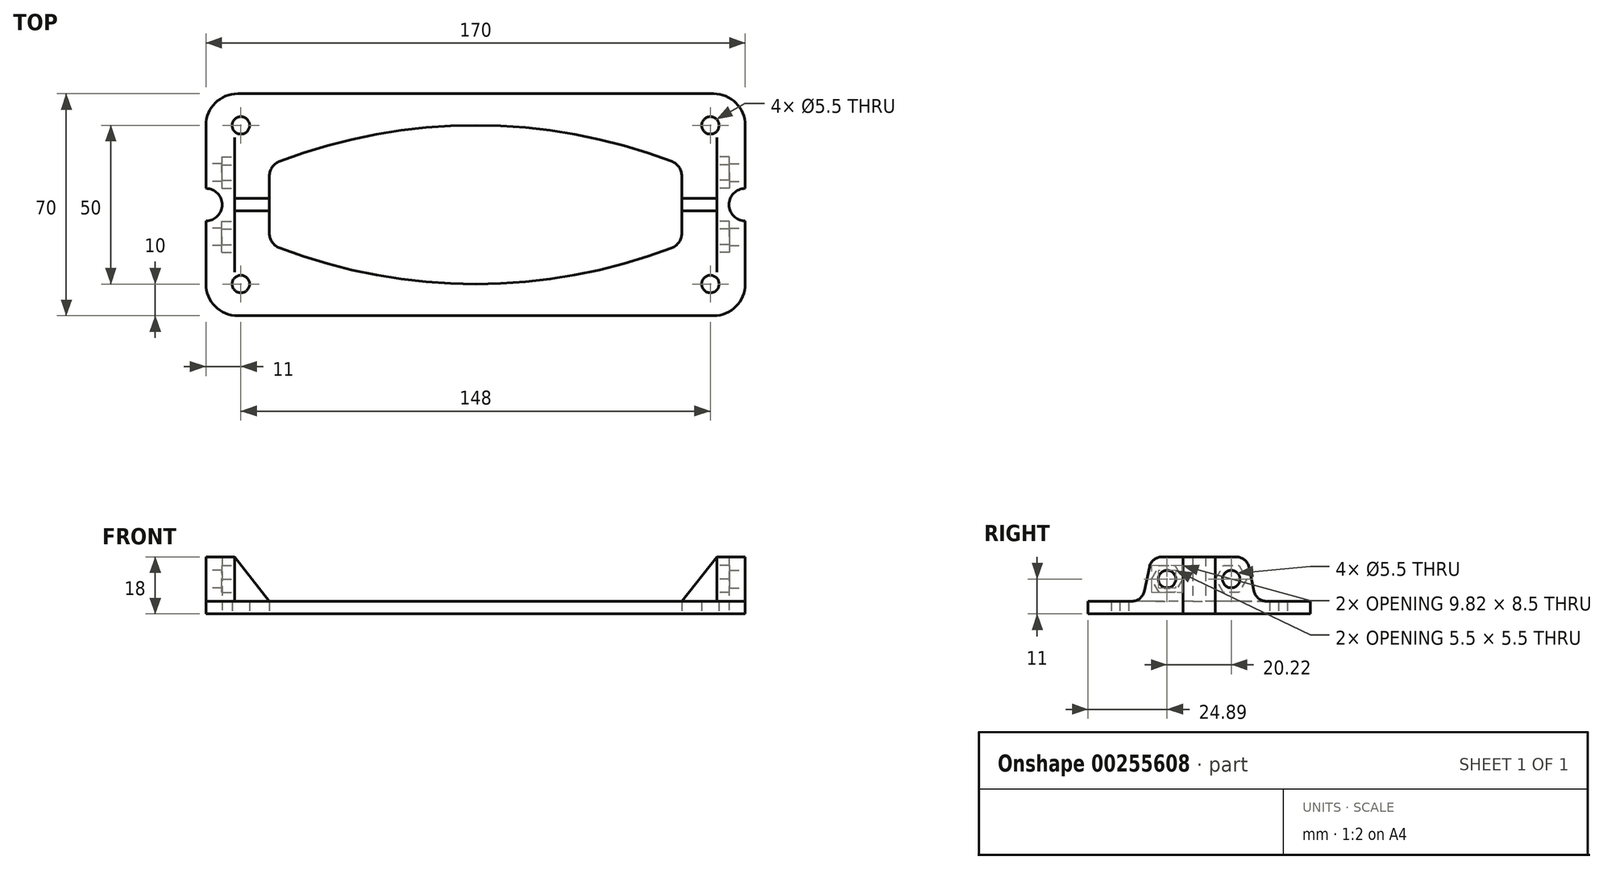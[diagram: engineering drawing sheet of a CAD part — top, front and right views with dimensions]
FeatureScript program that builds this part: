
annotation { "Feature Type Name" : "Feature", "Feature Type Description" : "" }
export const myFeature = defineFeature(function(context is Context, id is Id, definition is map)
    precondition{}
    {
        {
            var Q0;
            Q0=qCreatedBy(makeId("Top.planeOp"),FACE);
            var sketch = newSketch(context, id + "F0", { "sketchPlane" : qUnion([Q0])});
            skLineSegment(sketch, "E0.bottom", {"start": v(75, 35) * mm, "end": v(-75, 35) * mm});
            skLineSegment(sketch, "E0.top", {"start": v(75, -35) * mm, "end": v(-75, -35) * mm});
            skLineSegment(sketch, "E0.left", {"start": v(85, 25) * mm, "end": v(85, -25) * mm});
            skLineSegment(sketch, "E0.right", {"start": v(-85, 25) * mm, "end": v(-85, -25) * mm});
            skPoint(sketch, "E0.middle", {"position": v(0, 0) * mm});
            skLineSegment(sketch, "E1.left", {"start": v(65, 9) * mm, "end": v(65, -9) * mm});
            skLineSegment(sketch, "E1.right", {"start": v(-65, 9) * mm, "end": v(-65, -9) * mm});
            skLineSegment(sketch, "E2.bottom", {"start": v(-74, 25) * mm, "end": v(74, 25) * mm, "construction": true});
            skLineSegment(sketch, "E2.top", {"start": v(-74, -25) * mm, "end": v(74, -25) * mm, "construction": true});
            skLineSegment(sketch, "E2.left", {"start": v(-74, 25) * mm, "end": v(-74, -25) * mm, "construction": true});
            skLineSegment(sketch, "E2.right", {"start": v(74, 25) * mm, "end": v(74, -25) * mm, "construction": true});
            skCircle(sketch, "E3", {"center": v(-74, 25) * mm, "radius": 2.75 * mm});
            skCircle(sketch, "E4", {"center": v(74, 25) * mm, "radius": 2.75 * mm});
            skCircle(sketch, "E5", {"center": v(74, -25) * mm, "radius": 2.75 * mm});
            skCircle(sketch, "E6", {"center": v(-74, -25) * mm, "radius": 2.75 * mm});
            skPoint(sketch, "E7.visualSharp", {"position": v(-85, 35) * mm});
            skArc(sketch, "E7.filletArc", {"start": v(-75, 35) * mm, "mid": v(-82.07, 32.07) * mm, "end": v(-85, 25) * mm});
            skPoint(sketch, "E8.visualSharp", {"position": v(-85, -35) * mm});
            skArc(sketch, "E8.filletArc", {"start": v(-85, -25) * mm, "mid": v(-82.07, -32.07) * mm, "end": v(-75, -35) * mm});
            skPoint(sketch, "E9.visualSharp", {"position": v(85, -35) * mm});
            skArc(sketch, "E9.filletArc", {"start": v(75, -35) * mm, "mid": v(82.07, -32.07) * mm, "end": v(85, -25) * mm});
            skPoint(sketch, "E10.visualSharp", {"position": v(85, 35) * mm});
            skArc(sketch, "E10.filletArc", {"start": v(85, 25) * mm, "mid": v(82.07, 32.07) * mm, "end": v(75, 35) * mm});
            skArc(sketch, "E11", {"start": v(61.77, 13.67) * mm, "mid": v(0, 25) * mm, "end": v(-61.77, 13.67) * mm});
            skArc(sketch, "E12", {"start": v(-61.77, -13.67) * mm, "mid": v(0, -25) * mm, "end": v(61.77, -13.67) * mm});
            skPoint(sketch, "E13.visualSharp", {"position": v(-65, 12.41) * mm});
            skArc(sketch, "E13.filletArc", {"start": v(-61.77, 13.67) * mm, "mid": v(-64.12, 11.84) * mm, "end": v(-65, 9) * mm});
            skPoint(sketch, "E14.visualSharp", {"position": v(-65, -12.41) * mm});
            skArc(sketch, "E14.filletArc", {"start": v(-65, -9) * mm, "mid": v(-64.12, -11.84) * mm, "end": v(-61.77, -13.67) * mm});
            skPoint(sketch, "E15.visualSharp", {"position": v(65, -12.41) * mm});
            skArc(sketch, "E15.filletArc", {"start": v(61.77, -13.67) * mm, "mid": v(64.12, -11.84) * mm, "end": v(65, -9) * mm});
            skPoint(sketch, "E16.visualSharp", {"position": v(65, 12.41) * mm});
            skArc(sketch, "E16.filletArc", {"start": v(65, 9) * mm, "mid": v(64.12, 11.84) * mm, "end": v(61.77, 13.67) * mm});
            skSolve(sketch);
        }
        {
            var Q0;
            Q0=makeQuery(id+"F0.imprint","IMPRINT",FACE,{"disambiguationData":[TD([[makeQuery(id+"F0.imprint","IMPRINT",EDGE,{"derivedFrom":sQuery(id+"F0.wireOp",EDGE,"E0.bottom")}),1.0]])]});
            extrude(context, id + "F1", {"entities" : qUnion([Q0]), "depth" : 4 * mm});
        }
        {
            var Q0;
            Q0=makeQuery(id+"F1.opExtrude","SWEPT_FACE",FACE,{"disambiguationData":[OSD([sQuery(id+"F0.wireOp",EDGE,"E0.right")])]});
            var sketch = newSketch(context, id + "F2", { "sketchPlane" : qUnion([Q0])});
            skArc(sketch, "E17", {"start": v(-21.23, 4) * mm, "mid": v(-18.71, 4.89) * mm, "end": v(-17.32, 7.16) * mm});
            skArc(sketch, "E18", {"start": v(-11.76, 18) * mm, "mid": v(-14.28, 17.11) * mm, "end": v(-15.68, 14.84) * mm});
            skLineSegment(sketch, "E19", {"start": v(-17.32, 7.16) * mm, "end": v(-15.68, 14.84) * mm});
            skLineSegment(sketch, "E20", {"start": v(-11.76, 18) * mm, "end": v(11.77, 18) * mm});
            skArc(sketch, "E21.MirrorCS", {"start": v(21.23, 4) * mm, "mid": v(18.71, 4.89) * mm, "end": v(17.32, 7.16) * mm});
            skLineSegment(sketch, "E22.MirrorCS", {"start": v(17.32, 7.16) * mm, "end": v(15.68, 14.84) * mm});
            skArc(sketch, "E23.MirrorCS", {"start": v(11.77, 18) * mm, "mid": v(14.28, 17.11) * mm, "end": v(15.68, 14.84) * mm});
            skCircle(sketch, "E24", {"center": v(-10.1, 11) * mm, "radius": 2.75 * mm});
            skCircle(sketch, "E25.MirrorC", {"center": v(10.1, 11) * mm, "radius": 2.75 * mm});
            skSolve(sketch);
        }
        {
            var Q0;
            {var subQ0=sQuery(id+"F2.wireOp",EDGE,"E17");Q0=makeQuery(id+"F2.imprint","IMPRINT",FACE,{"disambiguationData":[TD([[makeQuery(id+"F2.imprint","IMPRINT",EDGE,{"derivedFrom":subQ0}),-1.0]])]});}
            extrude(context, id + "F3", {"entities" : qUnion([Q0]), "oppositeDirection" : true, "depth" : 9 * mm});
        }
        {
            var Q0;
            Q0=makeQuery(id+"F3.opExtrude","CAP_FACE",FACE,{"disambiguationData":[OSD([sQuery(id+"F0.wireOp",EDGE,"E0.right"),sQuery(id+"F2.wireOp",EDGE,"E17"),sQuery(id+"F2.wireOp",EDGE,"E18"),sQuery(id+"F2.wireOp",EDGE,"E19"),sQuery(id+"F2.wireOp",EDGE,"E20"),sQuery(id+"F2.wireOp",EDGE,"E21.MirrorCS"),sQuery(id+"F2.wireOp",EDGE,"E22.MirrorCS"),sQuery(id+"F2.wireOp",EDGE,"E23.MirrorCS"),sQuery(id+"F2.wireOp",EDGE,"E24"),sQuery(id+"F2.wireOp",EDGE,"E25.MirrorC")])],"isStart":false});
            var sketch = newSketch(context, id + "F4", { "sketchPlane" : qUnion([Q0])});
            skCircle(sketch, "E26.cCircle", {"center": v(-10.1, 11) * mm, "radius": 4.25 * mm, "construction": true});
            skLineSegment(sketch, "E26.0", {"start": v(-7.66, 15.25) * mm, "end": v(-5.2, 11) * mm});
            skLineSegment(sketch, "E26.1", {"start": v(-5.2, 11) * mm, "end": v(-7.66, 6.75) * mm});
            skLineSegment(sketch, "E26.2", {"start": v(-7.66, 6.75) * mm, "end": v(-12.56, 6.75) * mm});
            skLineSegment(sketch, "E26.3", {"start": v(-12.56, 6.75) * mm, "end": v(-15.02, 11) * mm});
            skLineSegment(sketch, "E26.4", {"start": v(-15.02, 11) * mm, "end": v(-12.56, 15.25) * mm});
            skLineSegment(sketch, "E26.5", {"start": v(-12.56, 15.25) * mm, "end": v(-7.66, 15.25) * mm});
            skPoint(sketch, "E26.0.midPoint", {"position": v(-6.43, 13.12) * mm});
            skCircle(sketch, "E27.cCircle", {"center": v(10.1, 11) * mm, "radius": 4.25 * mm, "construction": true});
            skLineSegment(sketch, "E27.0", {"start": v(7.66, 6.75) * mm, "end": v(5.2, 11) * mm});
            skLineSegment(sketch, "E27.1", {"start": v(5.2, 11) * mm, "end": v(7.66, 15.25) * mm});
            skLineSegment(sketch, "E27.2", {"start": v(7.66, 15.25) * mm, "end": v(12.56, 15.25) * mm});
            skLineSegment(sketch, "E27.3", {"start": v(12.56, 15.25) * mm, "end": v(15.02, 11) * mm});
            skLineSegment(sketch, "E27.4", {"start": v(15.02, 11) * mm, "end": v(12.56, 6.75) * mm});
            skLineSegment(sketch, "E27.5", {"start": v(12.56, 6.75) * mm, "end": v(7.66, 6.75) * mm});
            skPoint(sketch, "E27.0.midPoint", {"position": v(6.43, 8.87) * mm});
            skSolve(sketch);
        }
        {
            var Q0;
            Q0 = qSketchRegion(id + "F4", true);
            extrude(context, id + "F5", {"entities" : qUnion([Q0]), "operationType" : NewBodyOperationType.REMOVE, "oppositeDirection" : true, "depth" : 4 * mm});
        }
        {
            var Q0;
            Q0=makeQuery(id+"F3.opExtrude","SWEPT_BODY",BODY,{"disambiguationData":[OSD([sQuery(id+"F0.wireOp",EDGE,"E0.right"),sQuery(id+"F2.wireOp",EDGE,"E17"),sQuery(id+"F2.wireOp",EDGE,"E18"),sQuery(id+"F2.wireOp",EDGE,"E19"),sQuery(id+"F2.wireOp",EDGE,"E20"),sQuery(id+"F2.wireOp",EDGE,"E21.MirrorCS"),sQuery(id+"F2.wireOp",EDGE,"E22.MirrorCS"),sQuery(id+"F2.wireOp",EDGE,"E23.MirrorCS"),sQuery(id+"F2.wireOp",EDGE,"E24"),sQuery(id+"F2.wireOp",EDGE,"E25.MirrorC")])]});
            var Q1;
            Q1=qCreatedBy(makeId("Right.planeOp"),FACE);
            mirror(context, id + "F6", {"operationType" : NewBodyOperationType.ADD, "entities" : qUnion([Q0]), "mirrorPlane" : qUnion([Q1])});
        }
        {
            var Q0;
            Q0=makeQuery(id+"F1.opExtrude","CAP_FACE",FACE,{"disambiguationData":[OSD([sQuery(id+"F0.wireOp",EDGE,"E0.bottom"),sQuery(id+"F0.wireOp",EDGE,"E0.top"),sQuery(id+"F0.wireOp",EDGE,"E0.left"),sQuery(id+"F0.wireOp",EDGE,"E0.right"),sQuery(id+"F0.wireOp",EDGE,"E1.left"),sQuery(id+"F0.wireOp",EDGE,"E1.right"),sQuery(id+"F0.wireOp",EDGE,"E3"),sQuery(id+"F0.wireOp",EDGE,"E4"),sQuery(id+"F0.wireOp",EDGE,"E5"),sQuery(id+"F0.wireOp",EDGE,"E6"),sQuery(id+"F0.wireOp",EDGE,"E7.filletArc"),sQuery(id+"F0.wireOp",EDGE,"E8.filletArc"),sQuery(id+"F0.wireOp",EDGE,"E9.filletArc"),sQuery(id+"F0.wireOp",EDGE,"E10.filletArc"),sQuery(id+"F0.wireOp",EDGE,"E11"),sQuery(id+"F0.wireOp",EDGE,"E12"),sQuery(id+"F0.wireOp",EDGE,"E13.filletArc"),sQuery(id+"F0.wireOp",EDGE,"E14.filletArc"),sQuery(id+"F0.wireOp",EDGE,"E15.filletArc"),sQuery(id+"F0.wireOp",EDGE,"E16.filletArc")])],"isStart":true});
            var sketch = newSketch(context, id + "F7", { "sketchPlane" : qUnion([Q0])});
            skCircle(sketch, "E28", {"center": v(-85, 0) * mm, "radius": 5.12 * mm});
            skCircle(sketch, "E29", {"center": v(85, 0) * mm, "radius": 5.12 * mm});
            skSolve(sketch);
        }
        {
            var Q0;
            Q0 = qSketchRegion(id + "F7", true);
            extrude(context, id + "F8", {"entities" : qUnion([Q0]), "operationType" : NewBodyOperationType.REMOVE, "endBound" : BoundingType.THROUGH_ALL, "oppositeDirection" : true, "depth" : 25 * mm});
        }
        {
            var Q0;
            Q0=qCreatedBy(makeId("Front.planeOp"),FACE);
            var sketch = newSketch(context, id + "F9", { "sketchPlane" : qUnion([Q0])});
            skLineSegment(sketch, "E30", {"start": v(-76, 18) * mm, "end": v(-65, 4) * mm});
            skLineSegment(sketch, "E31.MirrorCS", {"start": v(76, 18) * mm, "end": v(65, 4) * mm});
            skLineSegment(sketch, "E32", {"start": v(-76, 18) * mm, "end": v(-76, 4) * mm});
            skLineSegment(sketch, "E33", {"start": v(-76, 4) * mm, "end": v(-65, 4) * mm});
            skLineSegment(sketch, "E34", {"start": v(76, 18) * mm, "end": v(76, 4) * mm});
            skLineSegment(sketch, "E35", {"start": v(76, 4) * mm, "end": v(65, 4) * mm});
            skSolve(sketch);
        }
        {
            var Q0;
            Q0 = qSketchRegion(id + "F9", true);
            extrude(context, id + "F10", {"entities" : qUnion([Q0]), "operationType" : NewBodyOperationType.ADD, "endBound" : BoundingType.SYMMETRIC, "depth" : 4 * mm});
        }
    });
